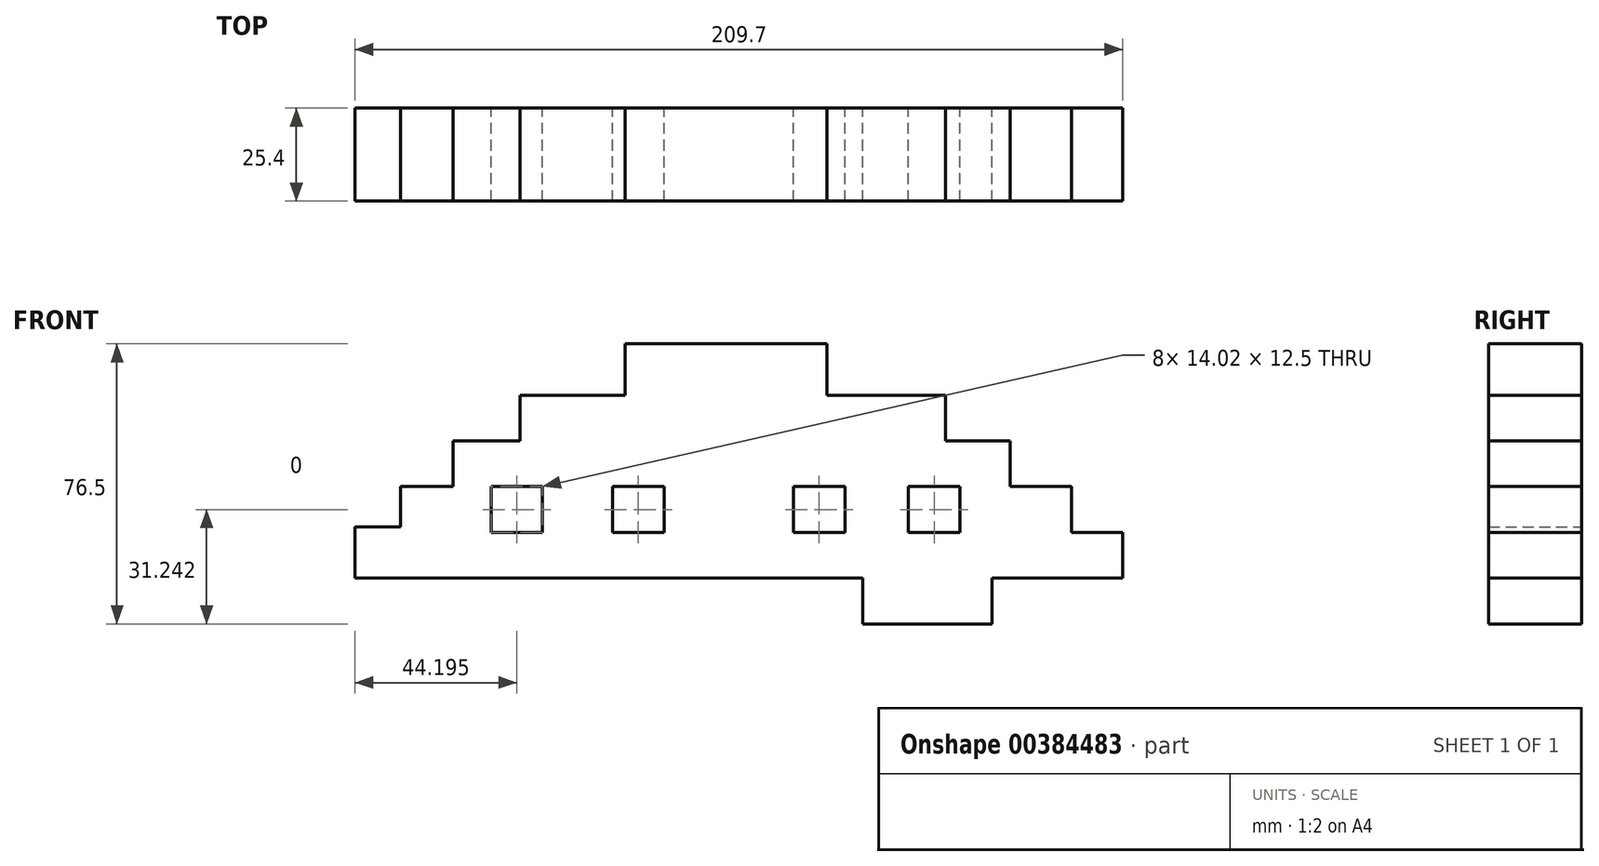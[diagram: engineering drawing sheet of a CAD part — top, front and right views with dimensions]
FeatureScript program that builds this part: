
annotation { "Feature Type Name" : "Feature", "Feature Type Description" : "" }
export const myFeature = defineFeature(function(context is Context, id is Id, definition is map)
    precondition{}
    {
        {
            var Q0;
            Q0=qCreatedBy(makeId("Front.planeOp"),FACE);
            var sketch = newSketch(context, id + "F0", { "sketchPlane" : qUnion([Q0])});
            skLineSegment(sketch, "E0.bottom", {"start": v(-24.08, 39.01) * mm, "end": v(31.09, 39.01) * mm});
            skLineSegment(sketch, "E0.left", {"start": v(-24.08, 39.01) * mm, "end": v(-24.08, 25) * mm});
            skLineSegment(sketch, "E0.right", {"start": v(31.09, 39.01) * mm, "end": v(31.09, 25) * mm});
            skLineSegment(sketch, "E1.bottom", {"start": v(-24.08, 25) * mm, "end": v(-52.73, 25) * mm});
            skLineSegment(sketch, "E1.right", {"start": v(-52.73, 25) * mm, "end": v(-52.73, 12.5) * mm});
            skLineSegment(sketch, "E2.bottom", {"start": v(31.09, 25) * mm, "end": v(63.4, 25) * mm});
            skLineSegment(sketch, "E2.right", {"start": v(63.4, 25) * mm, "end": v(63.4, 12.5) * mm});
            skLineSegment(sketch, "E3.bottom", {"start": v(-52.73, 12.5) * mm, "end": v(-71.02, 12.5) * mm});
            skLineSegment(sketch, "E3.right", {"start": v(-71.02, 12.5) * mm, "end": v(-71.02, 0) * mm});
            skLineSegment(sketch, "E4.bottom", {"start": v(63.4, 12.5) * mm, "end": v(81.08, 12.5) * mm});
            skLineSegment(sketch, "E4.right", {"start": v(81.08, 12.5) * mm, "end": v(81.08, 0) * mm});
            skLineSegment(sketch, "E5.bottom", {"start": v(-71.02, 0) * mm, "end": v(-85.34, 0) * mm});
            skLineSegment(sketch, "E5.right", {"start": v(-85.34, 0) * mm, "end": v(-85.34, -10.97) * mm});
            skLineSegment(sketch, "E6.bottom", {"start": v(81.08, 0) * mm, "end": v(97.84, 0) * mm});
            skLineSegment(sketch, "E6.right", {"start": v(97.84, 0) * mm, "end": v(97.84, -12.5) * mm});
            skLineSegment(sketch, "E7.bottom", {"start": v(-85.34, -10.97) * mm, "end": v(-97.84, -10.97) * mm});
            skLineSegment(sketch, "E7.top", {"start": v(-85.34, -25) * mm, "end": v(-97.84, -25) * mm});
            skLineSegment(sketch, "E7.right", {"start": v(-97.84, -10.97) * mm, "end": v(-97.84, -25) * mm});
            skLineSegment(sketch, "E8.bottom", {"start": v(97.84, -12.5) * mm, "end": v(111.86, -12.5) * mm});
            skLineSegment(sketch, "E8.top", {"start": v(97.84, -25) * mm, "end": v(111.86, -25) * mm});
            skLineSegment(sketch, "E8.right", {"start": v(111.86, -12.5) * mm, "end": v(111.86, -25) * mm});
            skLineSegment(sketch, "E9", {"start": v(-85.34, -25) * mm, "end": v(97.84, -25) * mm});
            skLineSegment(sketch, "E10.bottom", {"start": v(-60.66, 0) * mm, "end": v(-46.63, 0) * mm});
            skLineSegment(sketch, "E10.top", {"start": v(-60.66, -12.5) * mm, "end": v(-46.63, -12.5) * mm});
            skLineSegment(sketch, "E10.left", {"start": v(-60.66, 0) * mm, "end": v(-60.66, -12.5) * mm});
            skLineSegment(sketch, "E10.right", {"start": v(-46.63, 0) * mm, "end": v(-46.63, -12.5) * mm});
            skPoint(sketch, "E11.firstSnap0", {"position": v(-53.64, 0) * mm});
            skPoint(sketch, "E11.oppositeSnap0", {"position": v(-53.64, -12.5) * mm});
            skLineSegment(sketch, "E11.bottom", {"start": v(-27.43, 0) * mm, "end": v(-13.41, 0) * mm});
            skLineSegment(sketch, "E11.top", {"start": v(-27.43, -12.5) * mm, "end": v(-13.41, -12.5) * mm});
            skLineSegment(sketch, "E11.left", {"start": v(-27.43, 0) * mm, "end": v(-27.43, -12.5) * mm});
            skLineSegment(sketch, "E11.right", {"start": v(-13.41, 0) * mm, "end": v(-13.41, -12.5) * mm});
            skLineSegment(sketch, "E12.bottom", {"start": v(21.95, 0) * mm, "end": v(35.97, 0) * mm});
            skLineSegment(sketch, "E12.top", {"start": v(21.95, -12.5) * mm, "end": v(35.97, -12.5) * mm});
            skLineSegment(sketch, "E12.left", {"start": v(21.95, 0) * mm, "end": v(21.95, -12.5) * mm});
            skLineSegment(sketch, "E12.right", {"start": v(35.97, 0) * mm, "end": v(35.97, -12.5) * mm});
            skLineSegment(sketch, "E13.bottom", {"start": v(53.34, 0) * mm, "end": v(67.36, 0) * mm});
            skLineSegment(sketch, "E13.top", {"start": v(53.34, -12.5) * mm, "end": v(67.36, -12.5) * mm});
            skLineSegment(sketch, "E13.left", {"start": v(53.34, 0) * mm, "end": v(53.34, -12.5) * mm});
            skLineSegment(sketch, "E13.right", {"start": v(67.36, 0) * mm, "end": v(67.36, -12.5) * mm});
            skLineSegment(sketch, "E14.bottom", {"start": v(-65.23, -25) * mm, "end": v(-29.87, -25) * mm});
            skLineSegment(sketch, "E14.top", {"start": v(-65.23, -37.5) * mm, "end": v(-29.87, -37.5) * mm});
            skLineSegment(sketch, "E14.left", {"start": v(-65.23, -25) * mm, "end": v(-65.23, -37.5) * mm});
            skLineSegment(sketch, "E14.right", {"start": v(-29.87, -25) * mm, "end": v(-29.87, -37.5) * mm});
            skLineSegment(sketch, "E15.bottom", {"start": v(40.84, -37.5) * mm, "end": v(76.2, -37.5) * mm});
            skLineSegment(sketch, "E15.top", {"start": v(40.84, -25) * mm, "end": v(76.2, -25) * mm});
            skLineSegment(sketch, "E15.left", {"start": v(40.84, -37.5) * mm, "end": v(40.84, -25) * mm});
            skLineSegment(sketch, "E15.right", {"start": v(76.2, -37.5) * mm, "end": v(76.2, -25) * mm});
            skLineSegment(sketch, "E16.bottom", {"start": v(-55.17, -37.5) * mm, "end": v(-41.15, -37.5) * mm});
            skLineSegment(sketch, "E16.top", {"start": v(-55.17, -49.99) * mm, "end": v(-41.15, -49.99) * mm});
            skLineSegment(sketch, "E16.left", {"start": v(-55.17, -37.5) * mm, "end": v(-55.17, -49.99) * mm});
            skLineSegment(sketch, "E16.right", {"start": v(-41.15, -37.5) * mm, "end": v(-41.15, -49.99) * mm});
            skLineSegment(sketch, "E17.bottom", {"start": v(52.73, -37.5) * mm, "end": v(66.75, -37.5) * mm});
            skLineSegment(sketch, "E17.top", {"start": v(52.73, -49.99) * mm, "end": v(66.75, -49.99) * mm});
            skLineSegment(sketch, "E17.left", {"start": v(52.73, -37.5) * mm, "end": v(52.73, -49.99) * mm});
            skLineSegment(sketch, "E17.right", {"start": v(66.75, -37.5) * mm, "end": v(66.75, -49.99) * mm});
            skPoint(sketch, "E18.oppositeSnap0", {"position": v(21.95, -6.25) * mm});
            skLineSegment(sketch, "E18.bottom", {"start": v(-13.41, -25) * mm, "end": v(21.95, -25) * mm});
            skLineSegment(sketch, "E18.top", {"start": v(-13.41, -37.5) * mm, "end": v(21.95, -37.5) * mm});
            skLineSegment(sketch, "E18.left", {"start": v(-13.41, -25) * mm, "end": v(-13.41, -37.5) * mm});
            skLineSegment(sketch, "E18.right", {"start": v(21.95, -25) * mm, "end": v(21.95, -37.5) * mm});
            skSolve(sketch);
        }
        {
            var Q0;
            Q0=makeQuery(id+"F0.imprint","IMPRINT",FACE,{"disambiguationData":[TD([[makeQuery(id+"F0.imprint","IMPRINT",EDGE,{"derivedFrom":sQuery(id+"F0.wireOp",EDGE,"E0.bottom")}),-1.0]])]});
            var Q1;
            Q1=makeQuery(id+"F0.imprint","IMPRINT",FACE,{"disambiguationData":[TD([[makeQuery(id+"F0.imprint","IMPRINT",EDGE,{"derivedFrom":sQuery(id+"F0.wireOp",EDGE,"E15.bottom")}),1.0]])]});
            var Q2;
            Q2=makeQuery(id+"F0.imprint","IMPRINT",FACE,{"disambiguationData":[TD([[makeQuery(id+"F0.imprint","IMPRINT",EDGE,{"derivedFrom":sQuery(id+"F0.wireOp",EDGE,"E14.bottom")}),-1.0]])]});
            var Q3;
            Q3=makeQuery(id+"F0.imprint","IMPRINT",FACE,{"disambiguationData":[TD([[makeQuery(id+"F0.imprint","IMPRINT",EDGE,{"derivedFrom":sQuery(id+"F0.wireOp",EDGE,"E16.bottom")}),-1.0]])]});
            var Q4;
            Q4=makeQuery(id+"F0.imprint","IMPRINT",FACE,{"disambiguationData":[TD([[makeQuery(id+"F0.imprint","IMPRINT",EDGE,{"derivedFrom":sQuery(id+"F0.wireOp",EDGE,"E18.bottom")}),-1.0]])]});
            var Q5;
            Q5=makeQuery(id+"F0.imprint","IMPRINT",FACE,{"disambiguationData":[TD([[makeQuery(id+"F0.imprint","IMPRINT",EDGE,{"derivedFrom":sQuery(id+"F0.wireOp",EDGE,"E17.bottom")}),-1.0]])]});
            extrude(context, id + "F1", {"entities" : qUnion([Q0, Q1, Q2, Q3, Q4, Q5]), "depth" : 25.4 * mm});
        }
    });
